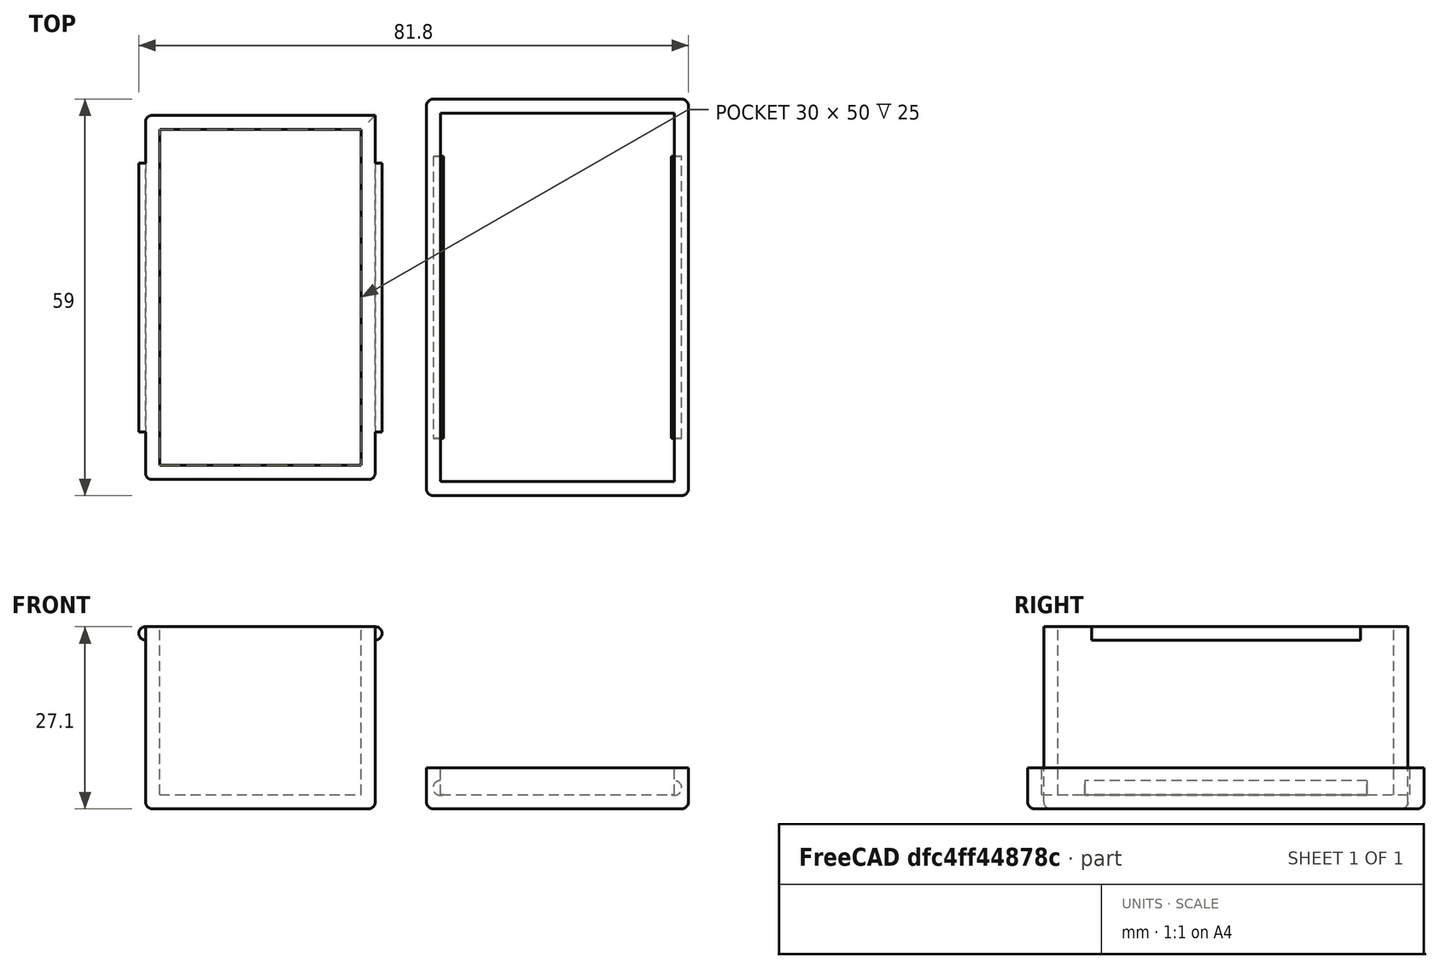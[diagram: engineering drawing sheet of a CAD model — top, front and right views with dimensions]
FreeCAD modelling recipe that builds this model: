
FCSTD DOCUMENT  (FreeCAD 0.21R33771 (Git))
Label: simple_3d_print_box
License: Creative Commons Attribution-NonCommercial-ShareAlike 4.0
LicenseURL: http://creativecommons.org/licenses/by-nc-sa/4.0/
objects: Part::Box×4, Part::Cut×4, Part::Cylinder×4, Part::Fillet×2, Part::MultiFuse×1
note: 15 computed .brp shape members not serialized (recipe doc carries the construction recipe); baked Part::Feature solids carry a one-line shape summary decoded from their .brp

FEATURE [Part::Box] case_inside
  AttacherType = Attacher::AttachEngine3D
  Height = 25
  Length = 30
  Width = 50
FEATURE [Part::Box] case_outside
  AttacherType = Attacher::AttachEngine3D
  Height = 27.1
  Length = 34.2
  Placement = pos=(-2.1,-2.1,-2.1) rot=(0,0,1;0rad)
  Width = 54.2
FEATURE [Part::Cut] Cut  label="case_cut_inside_outside"
  Base = -> case_outside
  Tool = -> case_inside
FEATURE [Part::Cylinder] tongue_left
  Angle = 360
  AttacherType = Attacher::AttachEngine3D
  FirstAngle = 0
  Height = 40
  Placement = pos=(-2.1,5,24) rot=(1,0,0;-1.5708rad)
  Radius = 1
  SecondAngle = 0
FEATURE [Part::Cylinder] lid_groove_left
  Angle = 360
  AttacherType = Attacher::AttachEngine3D
  FirstAngle = 0
  Height = 42
  Placement = pos=(-2.4,4,1) rot=(1,0,0;-1.5708rad)
  Radius = 1.1
  SecondAngle = 0
FEATURE [Part::Cylinder] tongue_right
  Angle = 360
  AttacherType = Attacher::AttachEngine3D
  FirstAngle = 0
  Height = 40
  Placement = pos=(32.1,5,24) rot=(1,0,0;-1.5708rad)
  Radius = 1
  SecondAngle = 0
FEATURE [Part::Cylinder] lid_groove_right
  Angle = 360
  AttacherType = Attacher::AttachEngine3D
  FirstAngle = 0
  Height = 42
  Placement = pos=(32.4,4,1) rot=(1,0,0;-1.5708rad)
  Radius = 1.1
  SecondAngle = 0
FEATURE [Part::MultiFuse] Fusion  label="fusion_case_tongues"
  Shapes = -> [Cut,tongue_left,tongue_right]
FEATURE [Part::Fillet] Fillet  label="case"
  Base = -> Fusion
  Edges = 7 edges r=1: [Edge18,Edge19,Edge20,Edge21,Edge23,Edge24,Edge28]
FEATURE [Part::Box] lid_inside
  AttacherType = Attacher::AttachEngine3D
  Height = 4
  Length = 34.8
  Placement = pos=(-2.4,-2.4,0) rot=(0,0,1;0rad)
  Width = 54.8
FEATURE [Part::Box] lid_outside
  AttacherType = Attacher::AttachEngine3D
  Height = 6.1
  Length = 39
  Placement = pos=(-4.5,-4.5,-2.1) rot=(0,0,1;0rad)
  Width = 59
FEATURE [Part::Cut] Cut001  label="lid_cut_inside_outside"
  Base = -> lid_outside
  Tool = -> lid_inside
FEATURE [Part::Cut] Cut002  label="lid_cut_groove"
  Base = -> Cut001
  Tool = -> lid_groove_right
FEATURE [Part::Cut] Cut003  label="lid_cut_groove_left"
  Base = -> Cut002
  Tool = -> lid_groove_left
FEATURE [Part::Fillet] Fillet001  label="lid"
  Base = -> Cut003
  Edges = 8 edges r=1: [Edge1,Edge3,Edge4,Edge5,Edge6,Edge14,Edge15,Edge16]
  Placement = pos=(44.2,0,0) rot=(0,0,1;0rad)
